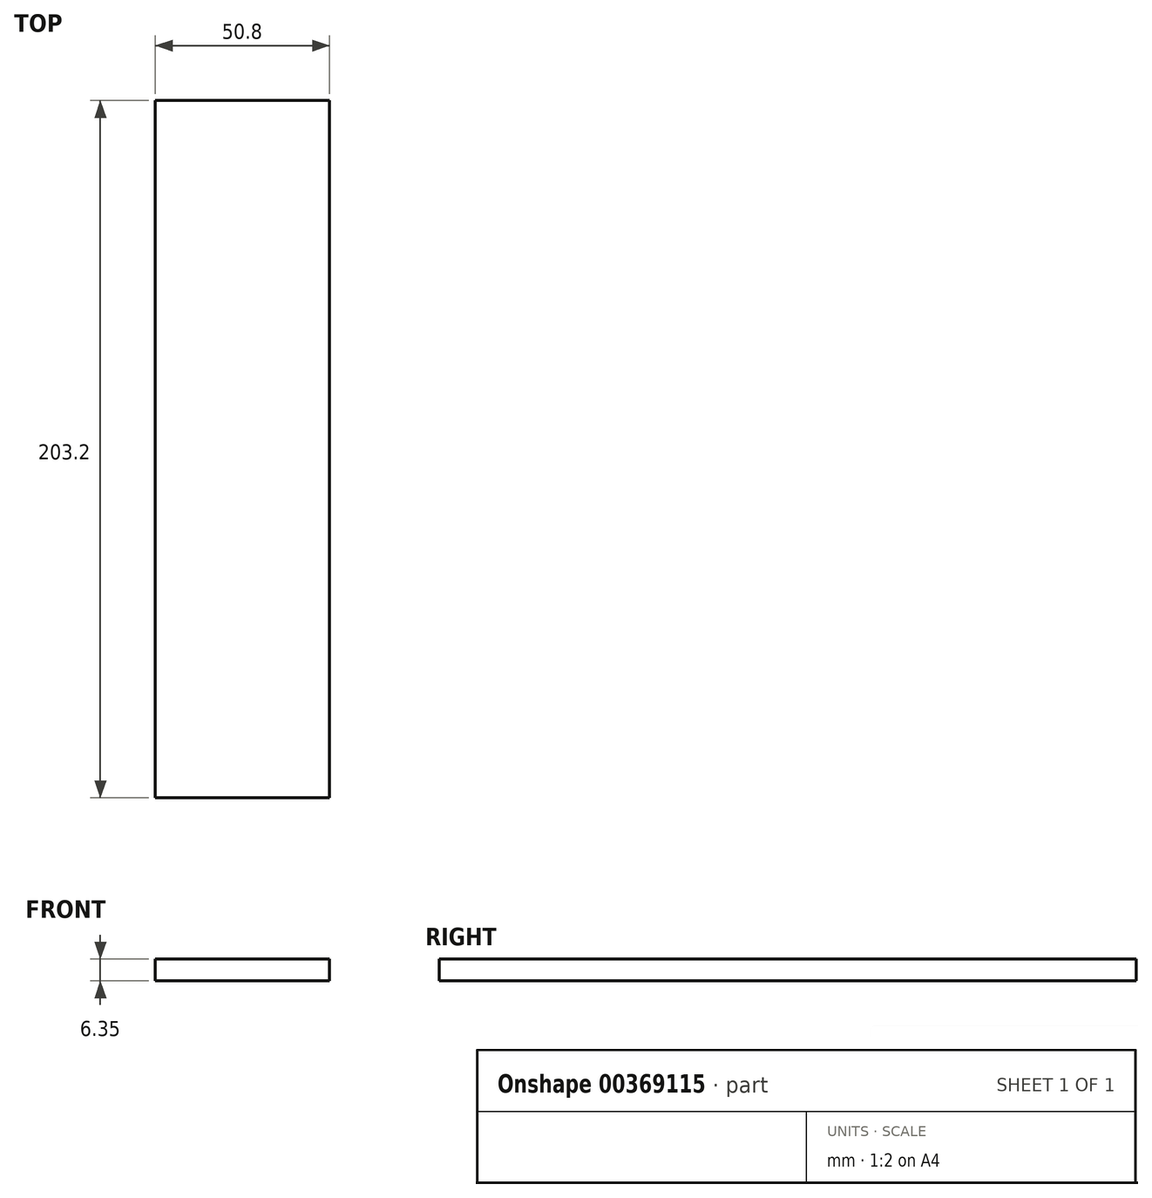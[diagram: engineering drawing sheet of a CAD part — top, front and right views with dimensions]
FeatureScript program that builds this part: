
annotation { "Feature Type Name" : "Feature", "Feature Type Description" : "" }
export const myFeature = defineFeature(function(context is Context, id is Id, definition is map)
    precondition{}
    {
        {
            var Q0;
            Q0=qCreatedBy(makeId("Top.planeOp"),FACE);
            var sketch = newSketch(context, id + "F0", { "sketchPlane" : qUnion([Q0])});
            skLineSegment(sketch, "E0.bottom", {"start": v(0, 0) * mm, "end": v(50.8, 0) * mm});
            skLineSegment(sketch, "E0.top", {"start": v(0, -203.2) * mm, "end": v(50.8, -203.2) * mm});
            skLineSegment(sketch, "E0.left", {"start": v(0, 0) * mm, "end": v(0, -203.2) * mm});
            skLineSegment(sketch, "E0.right", {"start": v(50.8, 0) * mm, "end": v(50.8, -203.2) * mm});
            skSolve(sketch);
        }
        {
            var Q0;
            Q0=makeQuery(id+"F0.imprint","IMPRINT",FACE,{"disambiguationData":[TD([[makeQuery(id+"F0.imprint","IMPRINT",EDGE,{"derivedFrom":sQuery(id+"F0.wireOp",EDGE,"E0.bottom")}),-1.0]])]});
            extrude(context, id + "F1", {"entities" : qUnion([Q0]), "depth" : 6.35 * mm});
        }
    });
